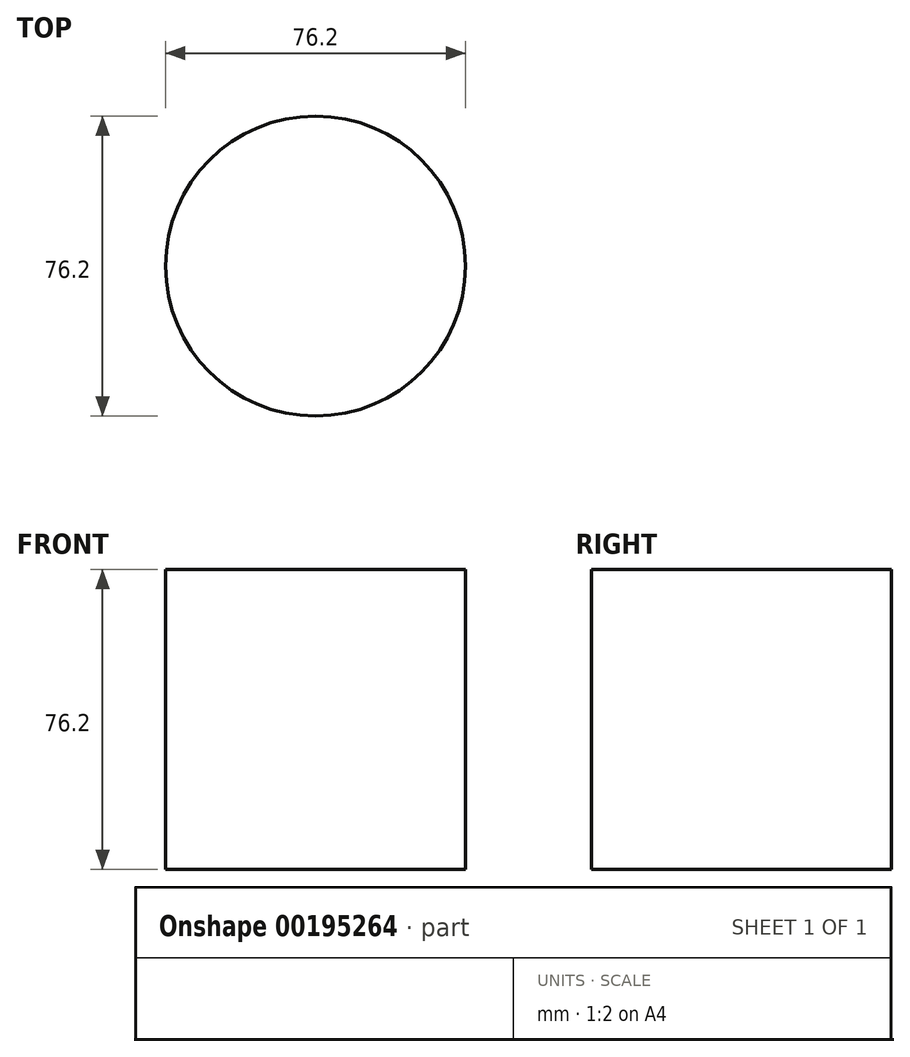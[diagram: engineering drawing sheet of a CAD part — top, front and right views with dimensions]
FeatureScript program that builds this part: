
annotation { "Feature Type Name" : "Feature", "Feature Type Description" : "" }
export const myFeature = defineFeature(function(context is Context, id is Id, definition is map)
    precondition{}
    {
        {
            var Q0;
            Q0=qCreatedBy(makeId("Top.planeOp"),FACE);
            var sketch = newSketch(context, id + "F0", { "sketchPlane" : qUnion([Q0])});
            skCircle(sketch, "E0", {"center": v(-24.46, -11.64) * mm, "radius": 38.1 * mm});
            skSolve(sketch);
        }
        {
            var Q0;
            Q0=makeQuery(id+"F0.imprint","IMPRINT",FACE,{"disambiguationData":[TD([[makeQuery(id+"F0.imprint","IMPRINT",EDGE,{"derivedFrom":sQuery(id+"F0.wireOp",EDGE,"E0")}),1.0]])]});
            extrude(context, id + "F1", {"entities" : qUnion([Q0]), "depth" : 76.2 * mm});
        }
    });
